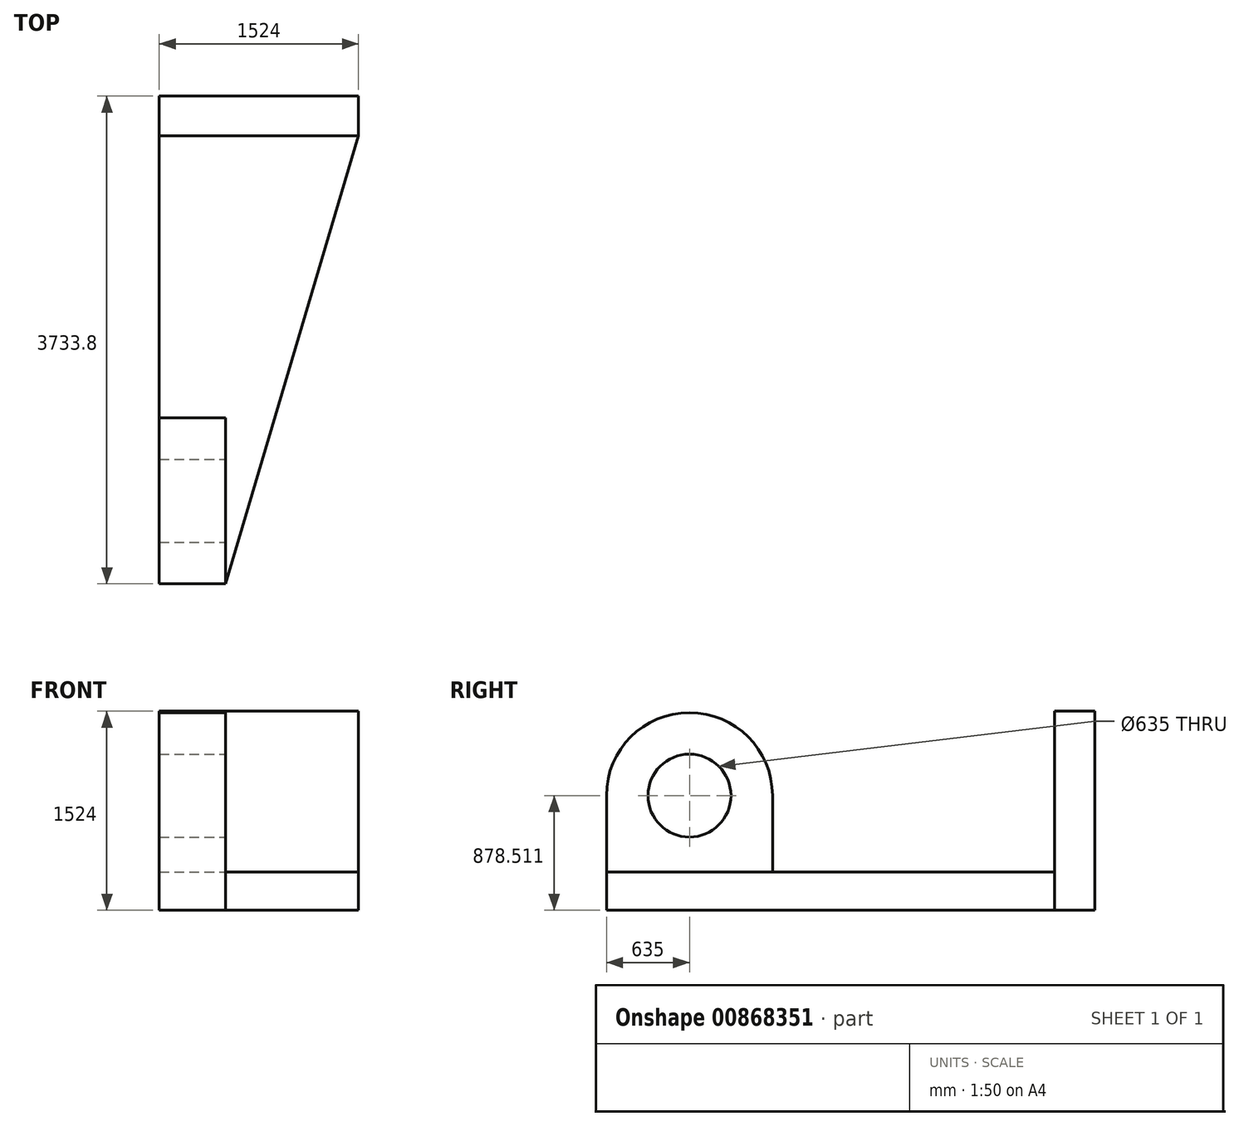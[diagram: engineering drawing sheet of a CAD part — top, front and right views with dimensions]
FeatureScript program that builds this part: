
annotation { "Feature Type Name" : "Feature", "Feature Type Description" : "" }
export const myFeature = defineFeature(function(context is Context, id is Id, definition is map)
    precondition{}
    {
        {
            var Q0;
            Q0=qCreatedBy(makeId("Front.planeOp"),FACE);
            var sketch = newSketch(context, id + "F0", { "sketchPlane" : qUnion([Q0])});
            skLineSegment(sketch, "E0.bottom", {"start": v(0, 0) * mm, "end": v(-1524, 0) * mm});
            skLineSegment(sketch, "E0.top", {"start": v(0, 1524) * mm, "end": v(-1524, 1524) * mm});
            skLineSegment(sketch, "E0.left", {"start": v(0, 0) * mm, "end": v(0, 1524) * mm});
            skLineSegment(sketch, "E0.right", {"start": v(-1524, 0) * mm, "end": v(-1524, 1524) * mm});
            skSolve(sketch);
        }
        {
            var Q0;
            Q0 = qSketchRegion(id + "F0", true);
            extrude(context, id + "F1", {"entities" : qUnion([Q0]), "depth" : 304.8 * mm, "offsetDistance" : 25.4 * mm});
        }
        {
            var Q0;
            Q0=makeQuery(id+"F1.opExtrude","CAP_FACE",FACE,{"disambiguationData":[OSD([sQuery(id+"F0.wireOp",EDGE,"E0.bottom"),sQuery(id+"F0.wireOp",EDGE,"E0.top"),sQuery(id+"F0.wireOp",EDGE,"E0.left"),sQuery(id+"F0.wireOp",EDGE,"E0.right")])],"isStart":false});
            var sketch = newSketch(context, id + "F2", { "sketchPlane" : qUnion([Q0])});
            skLineSegment(sketch, "E1.bottom", {"start": v(-1524, 0) * mm, "end": v(0, 0) * mm});
            skLineSegment(sketch, "E1.top", {"start": v(-1524, 294.31) * mm, "end": v(0, 294.31) * mm});
            skLineSegment(sketch, "E1.left", {"start": v(-1524, 0) * mm, "end": v(-1524, 294.31) * mm});
            skLineSegment(sketch, "E1.right", {"start": v(0, 0) * mm, "end": v(0, 294.31) * mm});
            skSolve(sketch);
        }
        {
            var Q0;
            Q0 = qSketchRegion(id + "F2", true);
            extrude(context, id + "F3", {"entities" : qUnion([Q0]), "operationType" : NewBodyOperationType.ADD, "depth" : 3429 * mm, "offsetDistance" : 25.4 * mm});
        }
        {
            var Q0;
            Q0=makeQuery(id+"F3.opExtrude","SWEPT_FACE",FACE,{"disambiguationData":[OSD([sQuery(id+"F2.wireOp",EDGE,"E1.top")])]});
            var sketch = newSketch(context, id + "F4", { "sketchPlane" : qUnion([Q0])});
            skLineSegment(sketch, "E2.bottom", {"start": v(-1524, -3733.8) * mm, "end": v(-1016, -3733.8) * mm});
            skLineSegment(sketch, "E2.top", {"start": v(-1524, -2463.8) * mm, "end": v(-1016, -2463.8) * mm});
            skLineSegment(sketch, "E2.left", {"start": v(-1524, -3733.8) * mm, "end": v(-1524, -2463.8) * mm});
            skLineSegment(sketch, "E2.right", {"start": v(-1016, -3733.8) * mm, "end": v(-1016, -2463.8) * mm});
            skSolve(sketch);
        }
        {
            var Q0;
            Q0=makeQuery(id+"F3.opExtrude","SWEPT_FACE",FACE,{"disambiguationData":[OSD([sQuery(id+"F2.wireOp",EDGE,"E1.top")])]});
            var sketch = newSketch(context, id + "F5", { "sketchPlane" : qUnion([Q0])});
            skLineSegment(sketch, "E3", {"start": v(-1016, -3733.8) * mm, "end": v(0, -304.8) * mm});
            skLineSegment(sketch, "E4", {"start": v(0, -304.8) * mm, "end": v(0, -3733.8) * mm});
            skLineSegment(sketch, "E5", {"start": v(0, -3733.8) * mm, "end": v(-1016, -3733.8) * mm});
            skSolve(sketch);
        }
        {
            var Q0;
            Q0 = qSketchRegion(id + "F5", true);
            extrude(context, id + "F6", {"entities" : qUnion([Q0]), "operationType" : NewBodyOperationType.REMOVE, "oppositeDirection" : true, "depth" : 84658.2 * mm, "offsetDistance" : 25.4 * mm});
        }
        {
            var Q0;
            Q0=makeQuery(id+"F4.imprint","IMPRINT",FACE,{"disambiguationData":[TD([[makeQuery(id+"F4.imprint","IMPRINT",EDGE,{"derivedFrom":sQuery(id+"F4.wireOp",EDGE,"E2.bottom")}),1.0]])]});
            extrude(context, id + "F7", {"entities" : qUnion([Q0]), "operationType" : NewBodyOperationType.ADD, "depth" : 584.2 * mm, "offsetDistance" : 25.4 * mm});
        }
        {
            var Q0;
            Q0=makeQuery(id+"F7.opExtrude","SWEPT_FACE",FACE,{"disambiguationData":[OSD([sQuery(id+"F4.wireOp",EDGE,"E2.right")])]});
            var sketch = newSketch(context, id + "F8", { "sketchPlane" : qUnion([Q0])});
            skCircle(sketch, "E6", {"center": v(-3098.8, 878.51) * mm, "radius": 635 * mm});
            skSolve(sketch);
        }
        {
            var Q0;
            {var subQ1=sQuery(id+"F4.wireOp",EDGE,"E2.right");var subQ2=makeQuery(id+"F7.opExtrude","CAP_EDGE",EDGE,{"disambiguationData":[OSD([subQ1])],"isStart":false});Q0=makeQuery(id+"F8.imprint","IMPRINT",FACE,{"disambiguationData":[TD([[makeQuery(id+"F8.imprint","IMPRINT",EDGE,{"derivedFrom":subQ2}),1.0]])]});}
            extrude(context, id + "F9", {"entities" : qUnion([Q0]), "operationType" : NewBodyOperationType.ADD, "oppositeDirection" : true, "depth" : 508 * mm, "offsetDistance" : 25.4 * mm});
        }
        {
            var Q0;
            {var subQ0=sQuery(id+"F4.wireOp",EDGE,"E2.right");Q0=makeQuery(id+"F9.boolean.opBoolean","MERGE",FACE,{"derivedFrom":[makeQuery(id+"F7.opExtrude","SWEPT_FACE",FACE,{"disambiguationData":[OSD([subQ0])]}),makeQuery(id+"F9.opExtrude","CAP_FACE",FACE,{"disambiguationData":[OSD([subQ0,sQuery(id+"F8.wireOp",EDGE,"E6")])],"isStart":true})]});}
            var sketch = newSketch(context, id + "F10", { "sketchPlane" : qUnion([Q0])});
            skCircle(sketch, "E7", {"center": v(-3098.8, 878.51) * mm, "radius": 317.5 * mm});
            skSolve(sketch);
        }
        {
            var Q0;
            Q0=makeQuery(id+"F10.imprint","IMPRINT",FACE,{"disambiguationData":[TD([[makeQuery(id+"F10.imprint","IMPRINT",EDGE,{"derivedFrom":sQuery(id+"F10.wireOp",EDGE,"E7")}),1.0]])]});
            extrude(context, id + "F11", {"entities" : qUnion([Q0]), "operationType" : NewBodyOperationType.REMOVE, "oppositeDirection" : true, "depth" : 1270 * mm, "offsetDistance" : 25.4 * mm});
        }
    });
